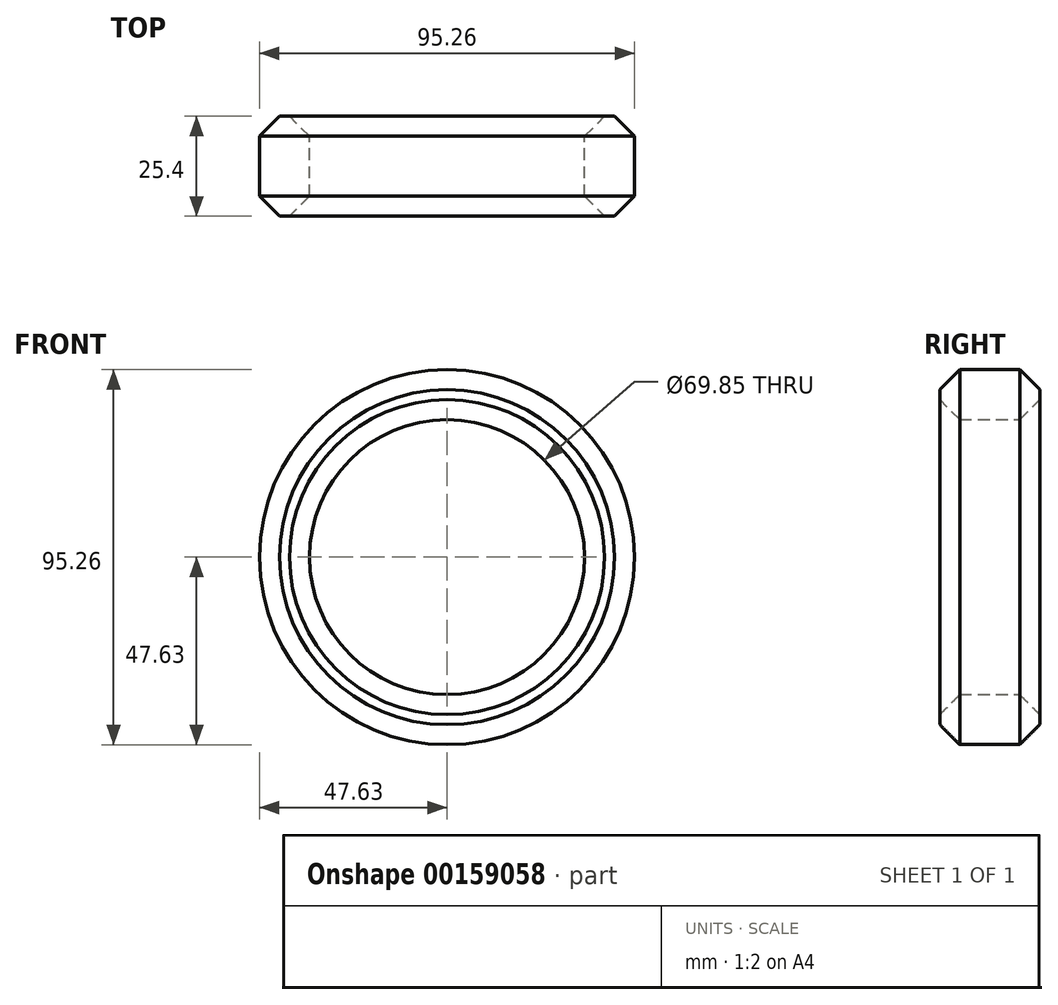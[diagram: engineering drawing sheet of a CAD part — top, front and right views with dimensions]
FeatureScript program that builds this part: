
annotation { "Feature Type Name" : "Feature", "Feature Type Description" : "" }
export const myFeature = defineFeature(function(context is Context, id is Id, definition is map)
    precondition{}
    {
        {
            var Q0;
            Q0=qCreatedBy(makeId("Front.planeOp"),FACE);
            var sketch = newSketch(context, id + "F0", { "sketchPlane" : qUnion([Q0])});
            skCircle(sketch, "E0", {"center": v(0, 0) * mm, "radius": 47.63 * mm});
            skCircle(sketch, "E1", {"center": v(0, 0) * mm, "radius": 34.93 * mm});
            skSolve(sketch);
        }
        {
            var Q0;
            Q0 = qSketchRegion(id + "F0", true);
            extrude(context, id + "F1", {"entities" : qUnion([Q0]), "endBound" : BoundingType.SYMMETRIC, "depth" : 25.4 * mm});
        }
        {
            var Q0;
            Q0=makeQuery(id+"F1.opExtrude","CAP_EDGE",EDGE,{"disambiguationData":[OSD([sQuery(id+"F0.wireOp",EDGE,"E0")])],"isStart":false});
            var Q1;
            Q1=makeQuery(id+"F1.opExtrude","CAP_EDGE",EDGE,{"disambiguationData":[OSD([sQuery(id+"F0.wireOp",EDGE,"E0")])],"isStart":true});
            var Q2;
            Q2=makeQuery(id+"F1.opExtrude","CAP_EDGE",EDGE,{"disambiguationData":[OSD([sQuery(id+"F0.wireOp",EDGE,"E1")])],"isStart":false});
            var Q3;
            Q3=makeQuery(id+"F1.opExtrude","CAP_EDGE",EDGE,{"disambiguationData":[OSD([sQuery(id+"F0.wireOp",EDGE,"E1")])],"isStart":true});
            chamfer(context, id + "F2", {"entities" : qUnion([Q0, Q1, Q2, Q3]), "width" : 5.08 * mm, "tangentPropagation" : true});
        }
    });
